# Revit family: METALFIRE_AVENUE_L_MF_GHE_1S
name_source: partatom
category: Mechanical Equipment
revit_build: Autodesk Revit 2017 (Build: 20160225_1515(x64)
units: mm (PartAtom-declared; Revit-internal decimal feet)

## family parameters
Always vertical = Yes
Cut with Voids When Loaded = No
Host = Wall
OmniClass Number = 23.75.00.00
OmniClass Title = Climate Control (HVAC)
Part Type = Normal
Room Calculation Point = Yes
Round Connector Dimension = Use Diameter
Shared = No

## types (1)
- 1300 x 950 mm
    BIM BADGE = https://bim.archiproducts.com
    Description = The Avenue represents the gas-fired high efficiency closed fireplaces in the Metalfire range.
    EFFICIENCY = 80.00%
    ENERGY EFFICIENCY CLASS = B
    FINISHING MATERIAL = Black painted vermiculite plates - Metalfire
    FRAME MATERIAL = Iron - Metalfire
    HEIGHT = 950 mm
    MATERIAL DESCRIPTION = Iron, galvanized steel and vermiculite plates
    Manufacturer = Metalfire
    Model = Avenue L
    OUTPUT = 11.4 kW
    OVERALL DEPTH = 625 mm
    OVERALL HEIGHT = 1450 mm
    OVERALL WIDTH = 1500 mm
    PRODUCT CODE = L MF 1300-95 GHE 1S
    PRODUCT SHEET = https://www.archiproducts.com
    SMOKE EXHAUST = Ø130/200 mm
    TECHNICAL SHEET = https://www.metalfire.eu
    URL = https://www.metalfire.eu
    WEIGHT = 180.00 kg
    WIDTH = 1300 mm

## geometry (parser evidence)
native form markers: Sweep x3
no freeform markers — native parametric forms only
